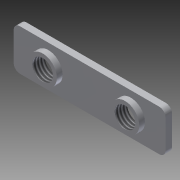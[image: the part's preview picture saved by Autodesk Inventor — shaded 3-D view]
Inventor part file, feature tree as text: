
AUTODESK INVENTOR PART (.ipt)
format: ipt  version: 2014 SP1 (Build 180222100, 222)  size: 110,592 bytes
history: native  units: in
note: dims shown in document units (in); Inventor stores cm internally (conversion verified against a paired STEP export)
features: extrude x2, thread x2, sketch x2, fillet x1
ambient origin geometry x8: Origin, YZ Plane, XZ Plane, XY Plane, X Axis, Y Axis, Z Axis, Center Point
bodies: Solid1 (feature_tree)
feature tree (7):
  extrude  "Extrusion1"  Depth=1.452in
  extrude  "Extrusion2"  Depth=0.0594in
  thread  "Thread1"  [1 undecoded]
  thread  "Thread2"  [1 undecoded]
  fillet  "Fillet1"  Radius=0.2717in
  sketch  "Sketch1"  dims[d0=0.3937in d1=1.452in]
  sketch  "Sketch2"  dims[d2=0.1969in d3=0.7874in d4=0.063in d5=0.0in d6=0.2717in d7=0.2717in d8=0.0551in d9=0.0in d10=0.3937in d11=0.0in d12=0.3937in d13=0.0in d14=0.0594in]
note: 2 required parameter values undecoded (feature->parameter linkage not recoverable at this tier; creation-order binding heuristic only, values carry confidence <= 0.55)
